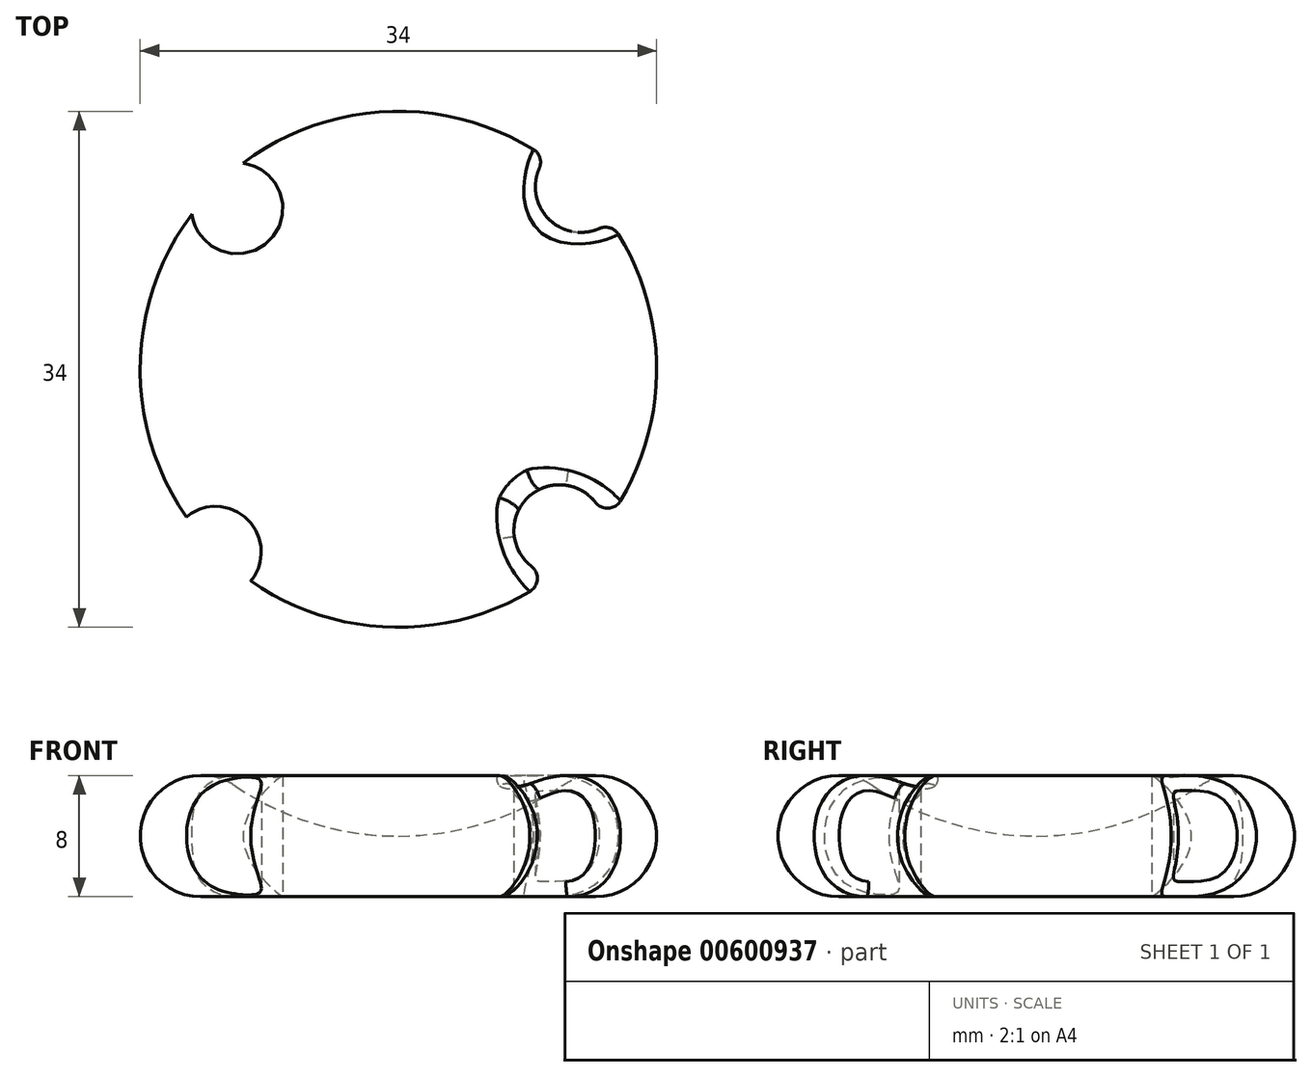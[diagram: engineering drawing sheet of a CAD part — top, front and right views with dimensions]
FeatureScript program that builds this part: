
annotation { "Feature Type Name" : "Feature", "Feature Type Description" : "" }
export const myFeature = defineFeature(function(context is Context, id is Id, definition is map)
    precondition{}
    {
        {
            var Q0;
            Q0=qCreatedBy(makeId("Front.planeOp"),FACE);
            var sketch = newSketch(context, id + "F0", { "sketchPlane" : qUnion([Q0])});
            skArc(sketch, "E0", {"start": v(-10.75, 7.3) * mm, "mid": v(-5.62, 4.85) * mm, "end": v(0, 4) * mm});
            skArc(sketch, "E1", {"start": v(-10.75, 7.3) * mm, "mid": v(-16.82, 5.18) * mm, "end": v(-13, 0) * mm});
            skLineSegment(sketch, "E2", {"start": v(0, 0) * mm, "end": v(-13, 0) * mm});
            skLineSegment(sketch, "E3", {"start": v(-13, 0) * mm, "end": v(0, 0) * mm});
            skLineSegment(sketch, "E4", {"start": v(0, 0) * mm, "end": v(0, 23.13) * mm});
            skLineSegment(sketch, "E5", {"start": v(-17, 0) * mm, "end": v(-17, 29.65) * mm});
            skSolve(sketch);
        }
        {
            var Q0;
            {var subQ0=sQuery(id+"F0.wireOp",EDGE,"E0");Q0=makeQuery(id+"F0.imprint","IMPRINT",FACE,{"disambiguationData":[TD([[makeQuery(id+"F0.imprint","IMPRINT",EDGE,{"derivedFrom":subQ0}),-1.0]])]});}
            var Q1;
            Q1=sQuery(id+"F0.wireOp",EDGE,"E4");
            revolve(context, id + "F1", {"entities" : qUnion([Q0]), "axis" : qUnion([Q1]), "revolveType" : RevolveType.FULL});
        }
        {
            var Q0;
            Q0=qCreatedBy(makeId("Top.planeOp"),FACE);
            var sketch = newSketch(context, id + "F2", { "sketchPlane" : qUnion([Q0])});
            skSolve(sketch);
        }
        {
            var Q0;
            Q0=qCreatedBy(makeId("Front.planeOp"),FACE);
            var sketch = newSketch(context, id + "F3", { "sketchPlane" : qUnion([Q0])});
            skCircle(sketch, "E6", {"center": v(-13, 4) * mm, "radius": 2.5 * mm});
            skLineSegment(sketch, "E7", {"start": v(0, 0) * mm, "end": v(0, 5.66) * mm});
            skSolve(sketch);
        }
        {
            var Q0;
            Q0=qSketchRegion(id+"F3",true);
            var Q1;
            Q1=sQuery(id+"F3.wireOp",EDGE,"E7");
            revolve(context, id + "F4", {"operationType" : NewBodyOperationType.ADD, "entities" : qUnion([Q0]), "axis" : qUnion([Q1]), "revolveType" : RevolveType.FULL});
        }
        {
            var Q0;
            Q0=qCreatedBy(makeId("Top.planeOp"),FACE);
            var sketch = newSketch(context, id + "F5", { "sketchPlane" : qUnion([Q0])});
            skLineSegment(sketch, "E8", {"start": v(0, 0) * mm, "end": v(0, -17) * mm});
            skEllipse(sketch, "E9", {"center": v(0, -17) * mm, "majorRadius": 4.33 * mm, "minorRadius": 2.48 * mm, "majorAxis": v(1, 0)});
            skEllipse(sketch, "E10", {"center": v(15.5, 0) * mm, "majorRadius": 2.48 * mm, "minorRadius": 4.33 * mm, "majorAxis": v(1, 0)});
            skLineSegment(sketch, "E11", {"start": v(0, 0) * mm, "end": v(-10.6, 10.6) * mm});
            skCircle(sketch, "E12", {"center": v(-10.6, 10.6) * mm, "radius": 3 * mm});
            skLineSegment(sketch, "E13", {"start": v(0, 0) * mm, "end": v(15.5, 0) * mm});
            skLineSegment(sketch, "E14", {"start": v(0, 0) * mm, "end": v(12.02, 12.02) * mm});
            skCircle(sketch, "E15", {"center": v(12.02, 12.02) * mm, "radius": 3 * mm});
            skLineSegment(sketch, "E16", {"start": v(0, 0) * mm, "end": v(10.6, -10.6) * mm});
            skCircle(sketch, "E17", {"center": v(10.6, -10.6) * mm, "radius": 3 * mm});
            skLineSegment(sketch, "E18", {"start": v(0, 0) * mm, "end": v(-12.02, -12.02) * mm});
            skCircle(sketch, "E19", {"center": v(-12.02, -12.02) * mm, "radius": 3 * mm});
            skLineSegment(sketch, "E20", {"start": v(0, 0) * mm, "end": v(-15.5, 0) * mm});
            skEllipse(sketch, "E21", {"center": v(-15.5, 0) * mm, "majorRadius": 2.48 * mm, "minorRadius": 4.33 * mm, "majorAxis": v(1, 0)});
            skLineSegment(sketch, "E22", {"start": v(0, 0) * mm, "end": v(0, 17) * mm});
            skEllipse(sketch, "E23", {"center": v(0, 17) * mm, "majorRadius": 4.33 * mm, "minorRadius": 2.48 * mm, "majorAxis": v(1, 0)});
            skSolve(sketch);
        }
        {
            var Q0;
            Q0=makeQuery(id+"F5.imprint","IMPRINT",FACE,{"disambiguationData":[TD([[makeQuery(id+"F5.imprint","IMPRINT",EDGE,{"derivedFrom":sQuery(id+"F5.wireOp",EDGE,"E15")}),1.0]])]});
            var Q1;
            Q1=makeQuery(id+"F5.imprint","IMPRINT",FACE,{"disambiguationData":[TD([[makeQuery(id+"F5.imprint","IMPRINT",EDGE,{"derivedFrom":sQuery(id+"F5.wireOp",EDGE,"E19")}),1.0]])]});
            var Q2;
            Q2=makeQuery(id+"F5.imprint","IMPRINT",FACE,{"disambiguationData":[TD([[makeQuery(id+"F5.imprint","IMPRINT",EDGE,{"derivedFrom":sQuery(id+"F5.wireOp",EDGE,"E17")}),1.0]])]});
            var Q3;
            Q3=makeQuery(id+"F5.imprint","IMPRINT",FACE,{"disambiguationData":[TD([[makeQuery(id+"F5.imprint","IMPRINT",EDGE,{"derivedFrom":sQuery(id+"F5.wireOp",EDGE,"E12")}),1.0]])]});
            extrude(context, id + "F6", {"entities" : qUnion([Q0, Q1, Q2, Q3]), "operationType" : NewBodyOperationType.REMOVE, "depth" : 25 * mm, "offsetDistance" : 25 * mm});
        }
        {
            var Q0;
            Q0=makeQuery(id+"F6.boolean.opBoolean","INTERSECT",EDGE,{"derivedFrom":[makeQuery(id+"F1.opRevolve","SWEPT_FACE",FACE,{"disambiguationData":[OSD([sQuery(id+"F0.wireOp",EDGE,"E1")])]}),makeQuery(id+"F6.opExtrude","SWEPT_FACE",FACE,{"disambiguationData":[OSD([sQuery(id+"F5.wireOp",EDGE,"E17")])]})]});
            var Q1;
            Q1=makeQuery(id+"F6.boolean.opBoolean","INTERSECT",EDGE,{"derivedFrom":[makeQuery(id+"F1.opRevolve","SWEPT_FACE",FACE,{"disambiguationData":[OSD([sQuery(id+"F0.wireOp",EDGE,"E1")])]}),makeQuery(id+"F6.opExtrude","SWEPT_FACE",FACE,{"disambiguationData":[OSD([sQuery(id+"F5.wireOp",EDGE,"E15")])]})]});
            fillet(context, id + "F7", {"entities" : qUnion([Q0, Q1]), "radius" : 1 * mm, "tangentPropagation" : true, "allowEdgeOverflow" : false});
        }
    });
